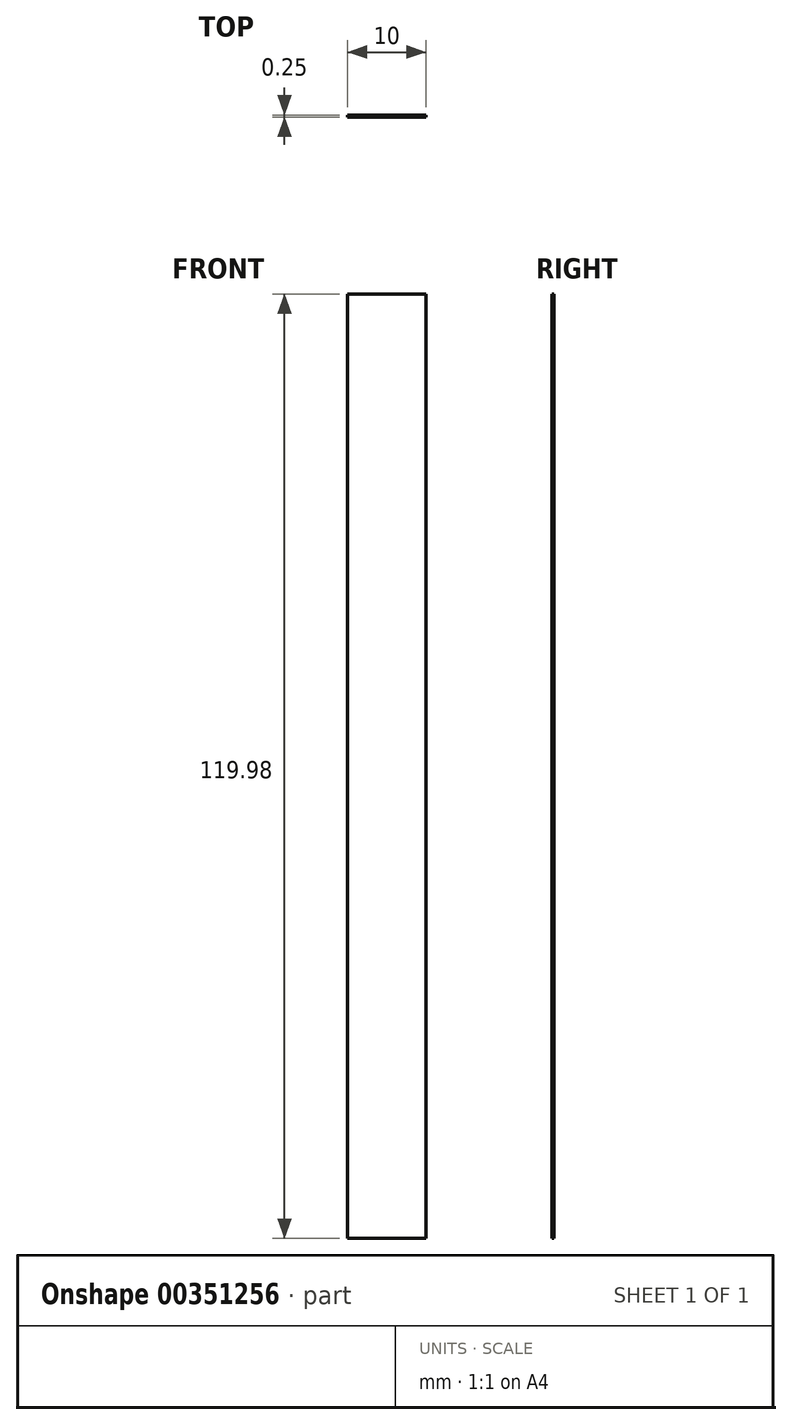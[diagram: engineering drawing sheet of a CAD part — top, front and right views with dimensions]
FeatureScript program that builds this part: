
annotation { "Feature Type Name" : "Feature", "Feature Type Description" : "" }
export const myFeature = defineFeature(function(context is Context, id is Id, definition is map)
    precondition{}
    {
        {
            var Q0;
            Q0=qCreatedBy(makeId("Front.planeOp"),FACE);
            var sketch = newSketch(context, id + "F0", { "sketchPlane" : qUnion([Q0])});
            skLineSegment(sketch, "E0.bottom", {"start": v(-26.43, 49.95) * mm, "end": v(-16.43, 49.95) * mm});
            skLineSegment(sketch, "E0.top", {"start": v(-26.43, -70.03) * mm, "end": v(-16.43, -70.03) * mm});
            skLineSegment(sketch, "E0.left", {"start": v(-26.43, 49.95) * mm, "end": v(-26.43, -70.03) * mm});
            skLineSegment(sketch, "E0.right", {"start": v(-16.43, 49.95) * mm, "end": v(-16.43, -70.03) * mm});
            skSolve(sketch);
        }
        {
            var Q0;
            Q0 = qSketchRegion(id + "F0", true);
            extrude(context, id + "F1", {"entities" : qUnion([Q0]), "depth" : 0.25 * mm});
        }
    });
